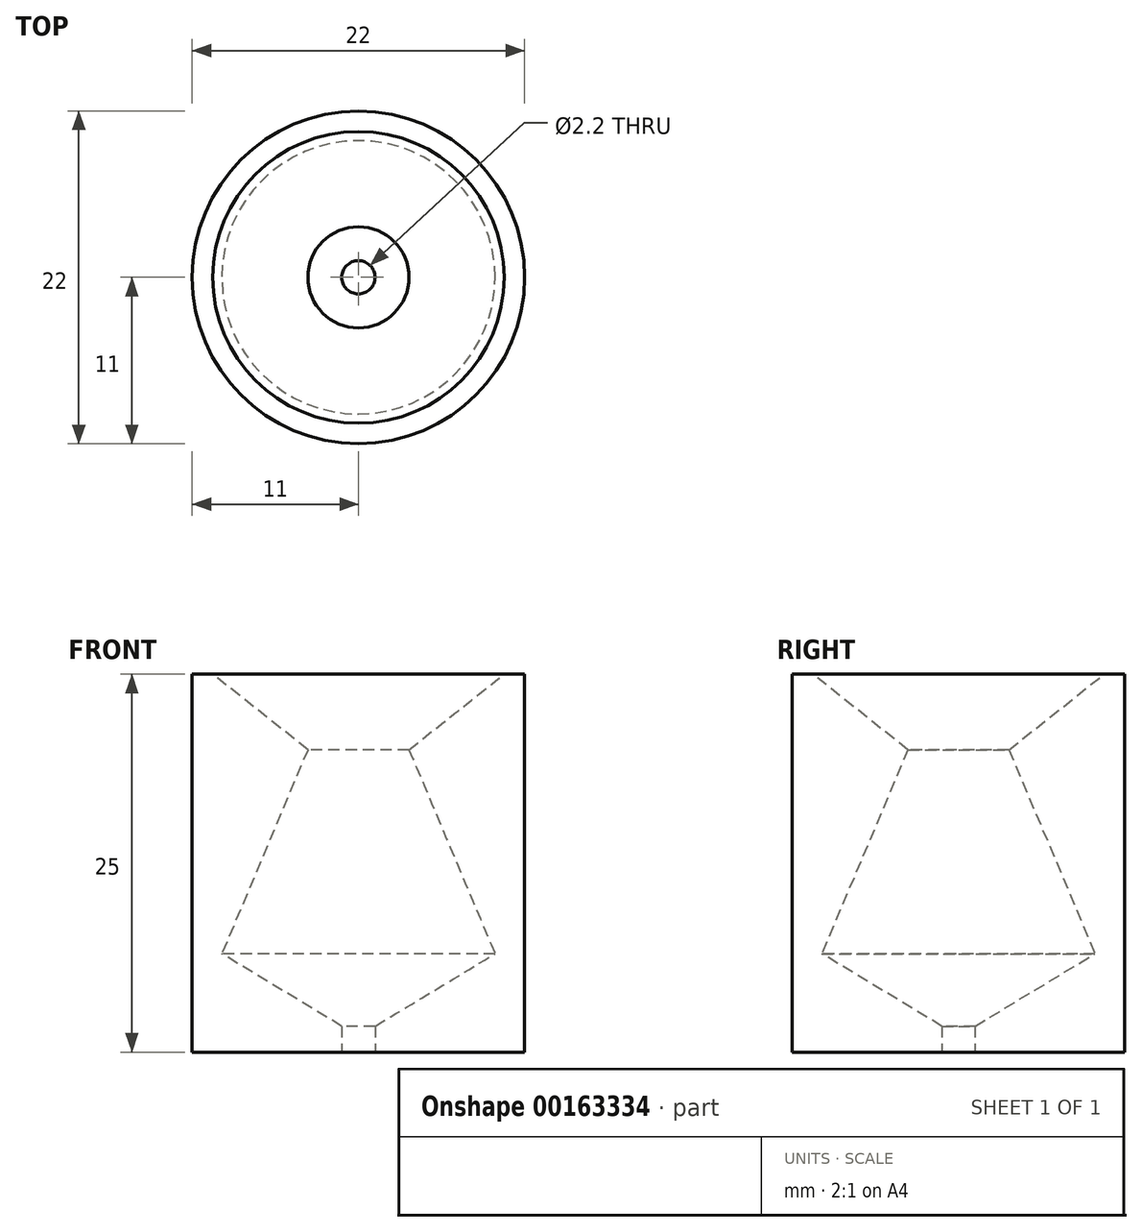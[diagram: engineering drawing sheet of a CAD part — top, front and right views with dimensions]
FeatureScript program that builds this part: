
annotation { "Feature Type Name" : "Feature", "Feature Type Description" : "" }
export const myFeature = defineFeature(function(context is Context, id is Id, definition is map)
    precondition{}
    {
        {
            var Q0;
            Q0=qCreatedBy(makeId("Top.planeOp"),FACE);
            var sketch = newSketch(context, id + "F0", { "sketchPlane" : qUnion([Q0])});
            skCircle(sketch, "E0", {"center": v(0, 0) * mm, "radius": 11 * mm});
            skCircle(sketch, "E1", {"center": v(0, 0) * mm, "radius": 1.1 * mm});
            skSolve(sketch);
        }
        {
            var Q0;
            Q0=makeQuery(id+"F0.imprint","IMPRINT",FACE,{"disambiguationData":[TD([[makeQuery(id+"F0.imprint","IMPRINT",EDGE,{"derivedFrom":sQuery(id+"F0.wireOp",EDGE,"E0")}),1.0]])]});
            extrude(context, id + "F1", {"entities" : qUnion([Q0]), "depth" : 25 * mm});
        }
        {
            var Q0;
            Q0=qCreatedBy(makeId("Front.planeOp"),FACE);
            var sketch = newSketch(context, id + "F2", { "sketchPlane" : qUnion([Q0])});
            skLineSegment(sketch, "E2", {"start": v(0, 1.06) * mm, "end": v(-9.04, 6.5) * mm});
            skLineSegment(sketch, "E3", {"start": v(-9.04, 6.5) * mm, "end": v(-3.35, 20) * mm});
            skLineSegment(sketch, "E4", {"start": v(-3.35, 20) * mm, "end": v(-12.08, 26.93) * mm});
            skLineSegment(sketch, "E5", {"start": v(-12.08, 26.93) * mm, "end": v(0, 29.97) * mm});
            skLineSegment(sketch, "E6", {"start": v(0, -0.74) * mm, "end": v(0, 36.65) * mm, "construction": true});
            skLineSegment(sketch, "E7", {"start": v(0, 29.97) * mm, "end": v(0, 1.06) * mm});
            skSolve(sketch);
        }
        {
            var Q0;
            Q0=makeQuery(id+"F2.imprint","IMPRINT",FACE,{"disambiguationData":[TD([[makeQuery(id+"F2.imprint","IMPRINT",EDGE,{"derivedFrom":sQuery(id+"F2.wireOp",EDGE,"E2")}),-1.0]])]});
            var Q1;
            Q1=sQuery(id+"F2.wireOp",EDGE,"E6");
            revolve(context, id + "F3", {"operationType" : NewBodyOperationType.REMOVE, "entities" : qUnion([Q0]), "axis" : qUnion([Q1]), "revolveType" : RevolveType.FULL, "oppositeDirection" : true});
        }
    });
